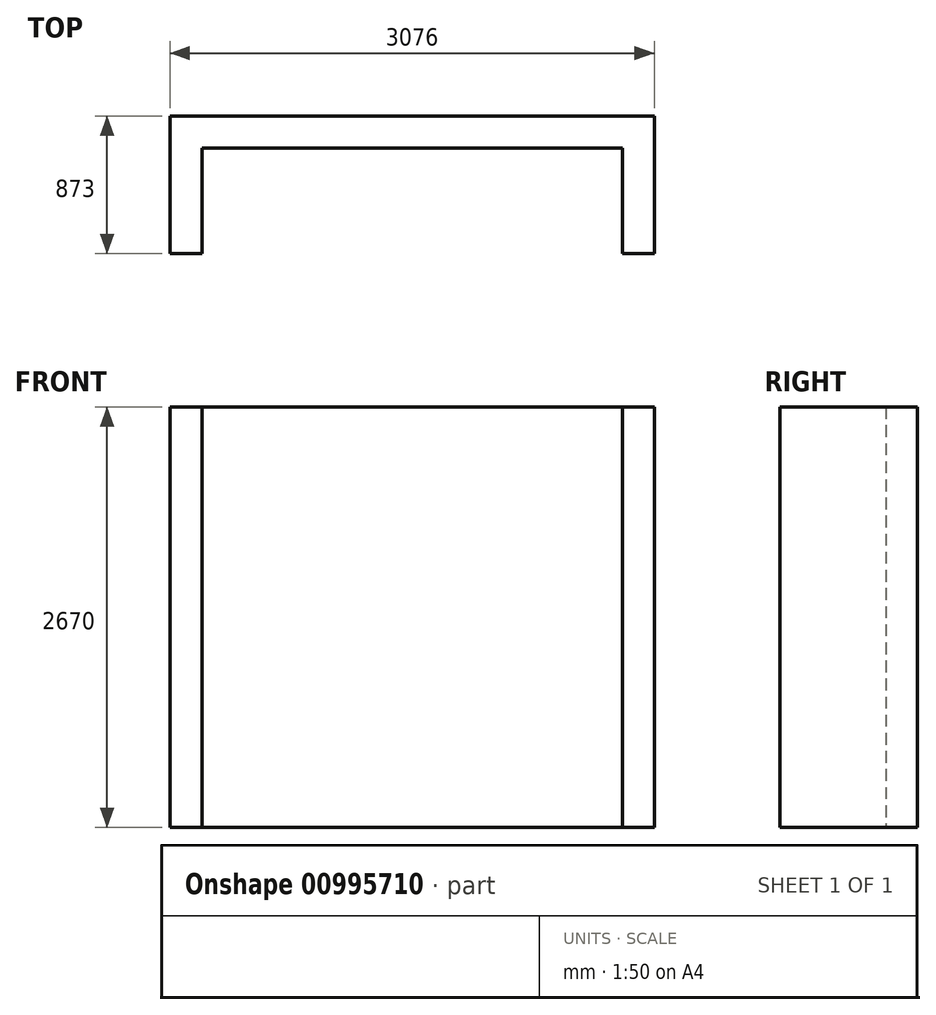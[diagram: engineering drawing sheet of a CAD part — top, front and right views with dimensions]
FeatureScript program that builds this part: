
annotation { "Feature Type Name" : "Feature", "Feature Type Description" : "" }
export const myFeature = defineFeature(function(context is Context, id is Id, definition is map)
    precondition{}
    {
        {
            var Q0;
            Q0=qCreatedBy(makeId("Top.planeOp"),FACE);
            var sketch = newSketch(context, id + "F0", { "sketchPlane" : qUnion([Q0])});
            skLineSegment(sketch, "E0", {"start": v(0, 335) * mm, "end": v(0, -335) * mm, "construction": true});
            skLineSegment(sketch, "E1", {"start": v(-1335, 0) * mm, "end": v(1335, 0) * mm, "construction": true});
            skLineSegment(sketch, "E2", {"start": v(-1335, -335) * mm, "end": v(-1335, 335) * mm});
            skLineSegment(sketch, "E3", {"start": v(-1335, 335) * mm, "end": v(1335, 335) * mm});
            skLineSegment(sketch, "E4", {"start": v(1335, 335) * mm, "end": v(1335, -335) * mm});
            skLineSegment(sketch, "E5", {"start": v(-1335, -335) * mm, "end": v(1335, -335) * mm, "construction": true});
            skLineSegment(sketch, "E6.0", {"start": v(1538, 538) * mm, "end": v(1538, -335) * mm});
            skLineSegment(sketch, "E6.1", {"start": v(-1538, 538) * mm, "end": v(1538, 538) * mm});
            skLineSegment(sketch, "E6.2", {"start": v(-1538, -335) * mm, "end": v(-1538, 538) * mm});
            skLineSegment(sketch, "E7", {"start": v(-1538, -335) * mm, "end": v(-1335, -335) * mm});
            skLineSegment(sketch, "E8", {"start": v(1538, -335) * mm, "end": v(1335, -335) * mm});
            skSolve(sketch);
        }
        {
            var Q0;
            Q0=makeQuery(id+"F0.imprint","IMPRINT",FACE,{"disambiguationData":[TD([[makeQuery(id+"F0.imprint","IMPRINT",EDGE,{"derivedFrom":sQuery(id+"F0.wireOp",EDGE,"E2")}),1.0]])]});
            extrude(context, id + "F1", {"entities" : qUnion([Q0]), "depth" : 2670 * mm, "offsetDistance" : 25.4 * mm});
        }
    });
